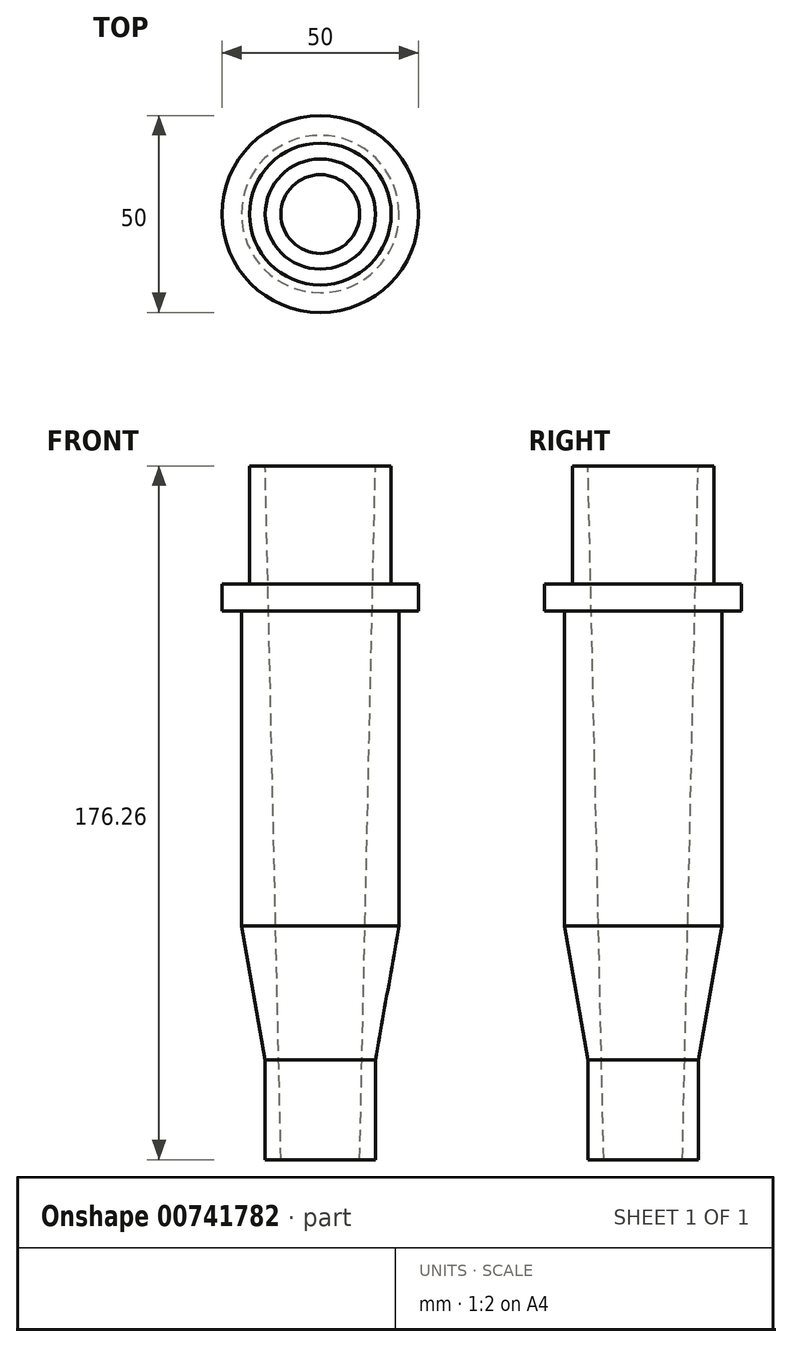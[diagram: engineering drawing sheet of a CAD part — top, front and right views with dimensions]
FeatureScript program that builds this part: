
annotation { "Feature Type Name" : "Feature", "Feature Type Description" : "" }
export const myFeature = defineFeature(function(context is Context, id is Id, definition is map)
    precondition{}
    {
        {
            var Q0;
            Q0=qCreatedBy(makeId("Front.planeOp"),FACE);
            var sketch = newSketch(context, id + "F0", { "sketchPlane" : qUnion([Q0])});
            skLineSegment(sketch, "E0", {"start": v(-14, 69.5) * mm, "end": v(-18, 69.5) * mm});
            skLineSegment(sketch, "E1", {"start": v(-18, 69.5) * mm, "end": v(-18, 39.5) * mm});
            skLineSegment(sketch, "E2", {"start": v(-10, -106.77) * mm, "end": v(-14, 69.5) * mm});
            skLineSegment(sketch, "E3", {"start": v(-20, 39.5) * mm, "end": v(-18, 39.5) * mm});
            skLineSegment(sketch, "E4", {"start": v(0, 77.75) * mm, "end": v(0, -122.25) * mm, "construction": true});
            skLineSegment(sketch, "E5", {"start": v(-14, -106.77) * mm, "end": v(-10, -106.77) * mm});
            skLineSegment(sketch, "E6", {"start": v(-20, -47.42) * mm, "end": v(-14, -81.45) * mm});
            skLineSegment(sketch, "E7", {"start": v(-14, -81.45) * mm, "end": v(-14, -106.77) * mm});
            skLineSegment(sketch, "E8", {"start": v(-10, -122.25) * mm, "end": v(-10, 77.75) * mm, "construction": true});
            skLineSegment(sketch, "E9", {"start": v(-10, -81.45) * mm, "end": v(-25.46, 6.24) * mm, "construction": true});
            skLineSegment(sketch, "E10", {"start": v(-20, -47.42) * mm, "end": v(-20, 32.58) * mm});
            skLineSegment(sketch, "E11", {"start": v(-20, 32.58) * mm, "end": v(-25, 32.58) * mm});
            skLineSegment(sketch, "E12", {"start": v(-25, 32.58) * mm, "end": v(-25, 39.5) * mm});
            skLineSegment(sketch, "E13", {"start": v(-25, 39.5) * mm, "end": v(-20, 39.5) * mm});
            skSolve(sketch);
        }
        {
            var Q0;
            Q0 = qSketchRegion(id + "F0", true);
            var Q1;
            Q1=sQuery(id+"F0.wireOp",EDGE,"E4");
            revolve(context, id + "F1", {"surfaceOperationType" : NewSurfaceOperationType.NEW, "entities" : qUnion([Q0]), "axis" : qUnion([Q1]), "revolveType" : RevolveType.FULL});
        }
    });
